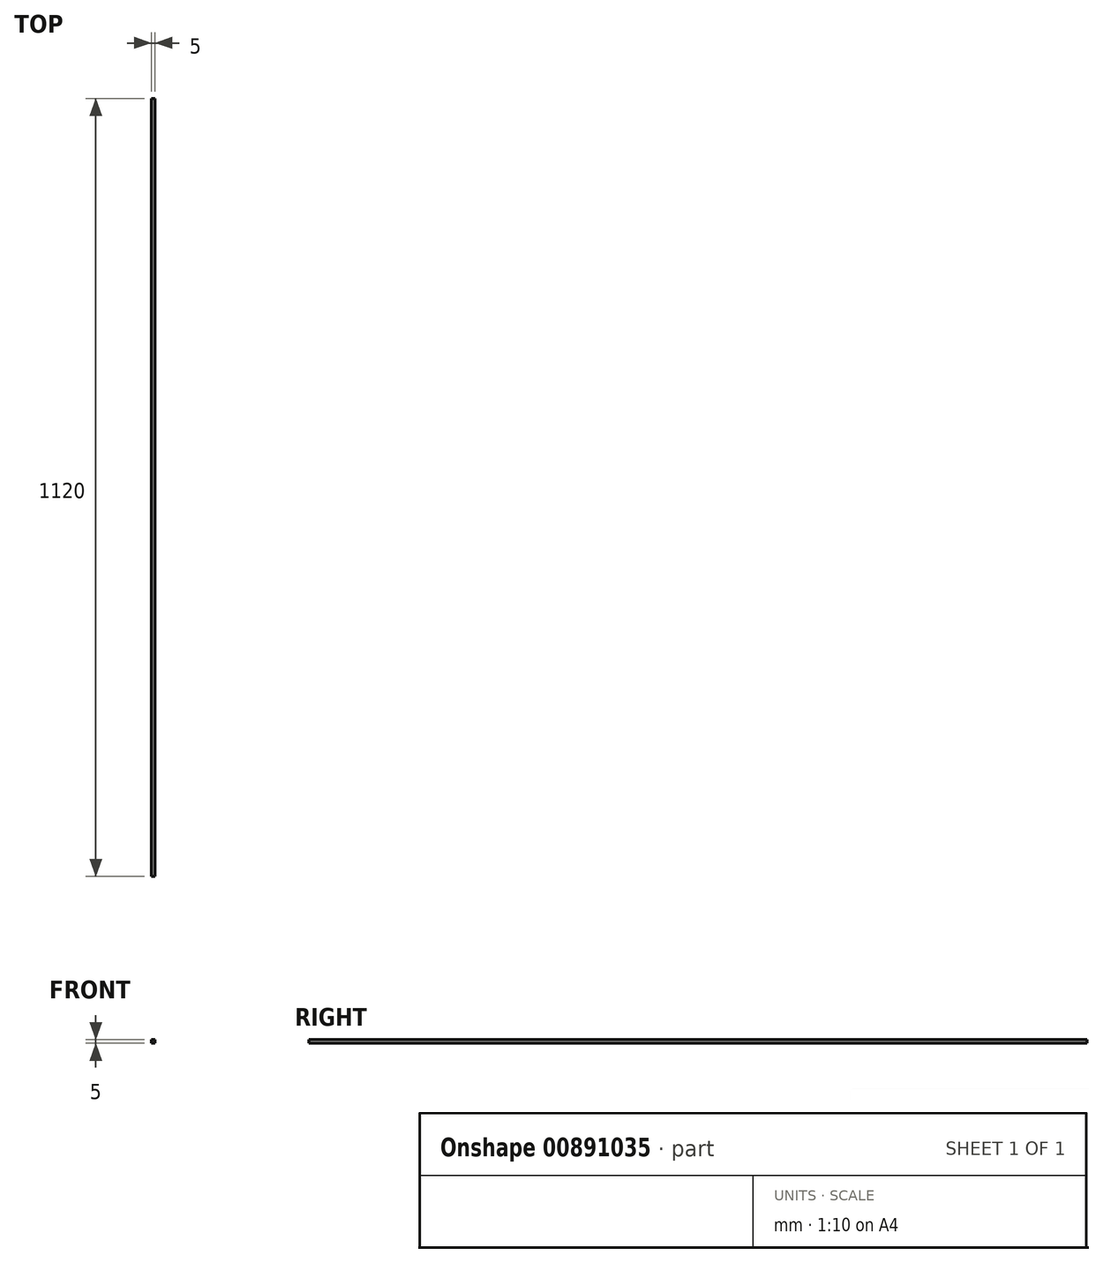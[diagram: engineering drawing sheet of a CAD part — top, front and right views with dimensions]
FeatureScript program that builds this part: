
annotation { "Feature Type Name" : "Feature", "Feature Type Description" : "" }
export const myFeature = defineFeature(function(context is Context, id is Id, definition is map)
    precondition{}
    {
        {
            var Q0;
            Q0=qCreatedBy(makeId("Front.planeOp"),FACE);
            var sketch = newSketch(context, id + "F0", { "sketchPlane" : qUnion([Q0])});
            skLineSegment(sketch, "E0.bottom", {"start": v(0, 0) * mm, "end": v(5, 0) * mm});
            skLineSegment(sketch, "E0.top", {"start": v(0, -5) * mm, "end": v(5, -5) * mm});
            skLineSegment(sketch, "E0.left", {"start": v(0, 0) * mm, "end": v(0, -5) * mm});
            skLineSegment(sketch, "E0.right", {"start": v(5, 0) * mm, "end": v(5, -5) * mm});
            skSolve(sketch);
        }
        {
            var Q0;
            Q0=makeQuery(id+"F0.imprint","IMPRINT",FACE,{"disambiguationData":[TD([[makeQuery(id+"F0.imprint","IMPRINT",EDGE,{"derivedFrom":sQuery(id+"F0.wireOp",EDGE,"E0.bottom")}),-1.0]])]});
            extrude(context, id + "F1", {"entities" : qUnion([Q0]), "depth" : 1120 * mm, "offsetDistance" : 25 * mm});
        }
    });
